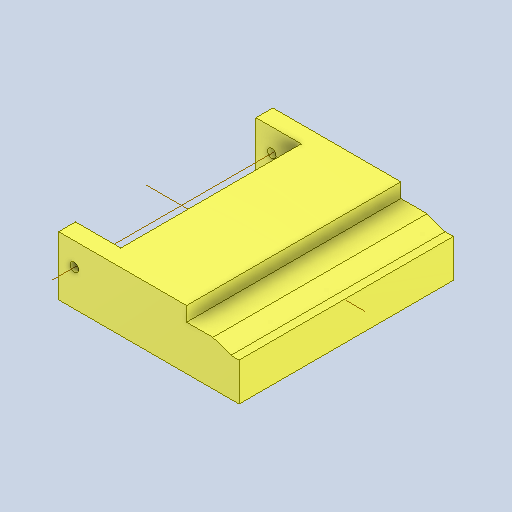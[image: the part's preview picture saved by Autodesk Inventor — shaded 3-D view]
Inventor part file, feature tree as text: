
AUTODESK INVENTOR PART (.ipt)
format: ipt  version: 2025 (Build 290162000, 162)  size: 137,728 bytes
history: native  units: mm
features: other x3, extrude x3, sketch x3
ambient origin geometry x8: Origin, YZ Plane, XZ Plane, XY Plane, X Axis, Y Axis, Z Axis, Center Point
bodies: Body1 (feature_tree)
feature tree (9):
  parser-record x1  (decoder bookkeeping rows leaked as tree rows — omitted from the tree; the rows remain in map.json)
  other  "實體1"
  extrude  "擠出1"  Depth=110.0mm
  extrude  "擠出2"  Depth=48.0mm
  extrude  "擠出3"  Depth=180.0mm
  sketch  "草圖1"
  sketch  "草圖2"
  sketch  "草圖3"
  other  "投影切割邊1"
note: 1 file-system path scrubbed to <path> (originals preserved in map.json)
